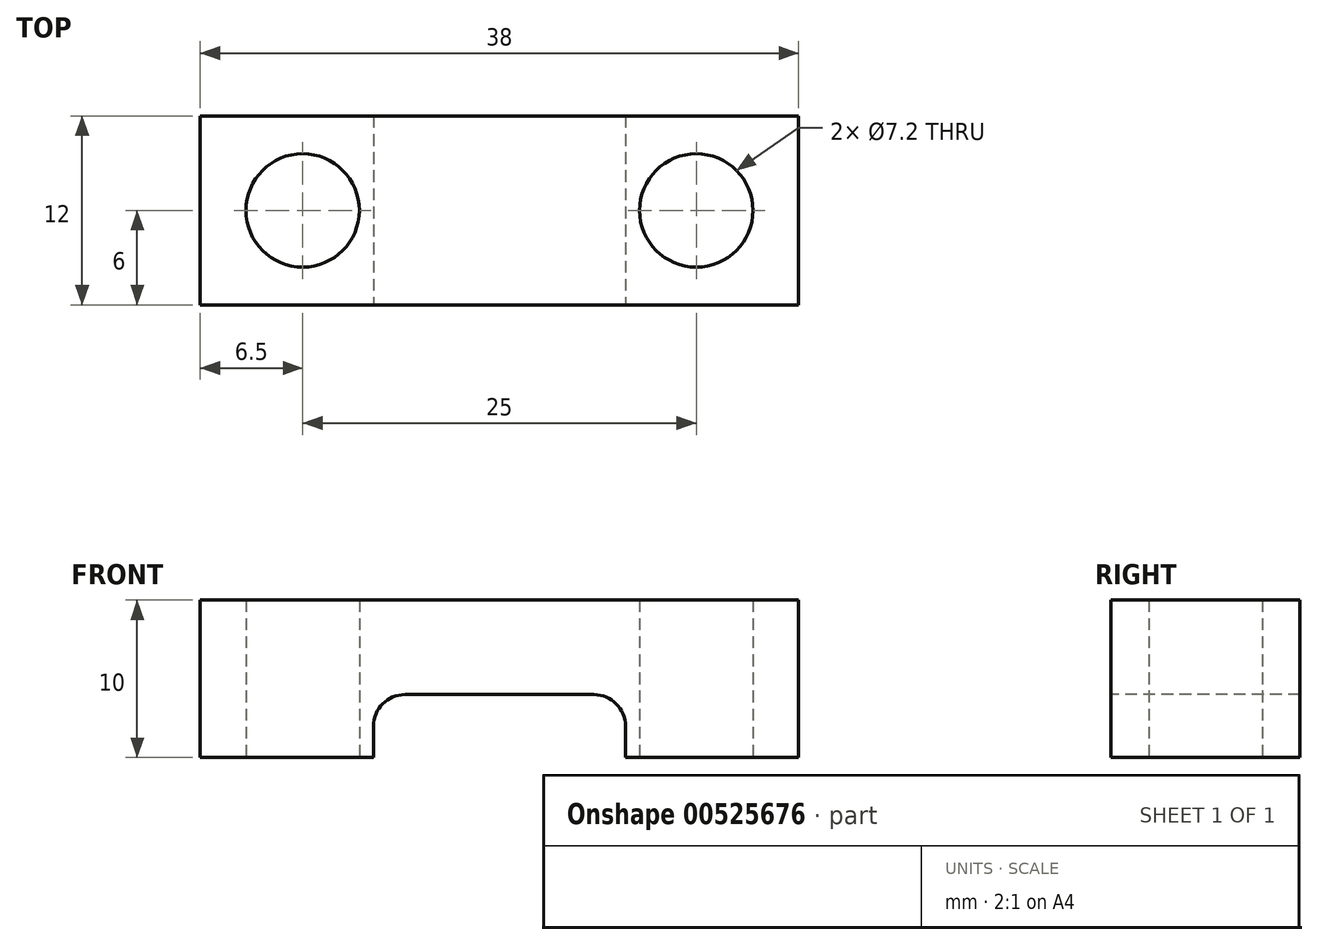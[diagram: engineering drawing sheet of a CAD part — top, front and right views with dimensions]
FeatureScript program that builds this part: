
annotation { "Feature Type Name" : "Feature", "Feature Type Description" : "" }
export const myFeature = defineFeature(function(context is Context, id is Id, definition is map)
    precondition{}
    {
        {
            var Q0;
            Q0=qCreatedBy(makeId("Top.planeOp"),FACE);
            var sketch = newSketch(context, id + "F0", { "sketchPlane" : qUnion([Q0])});
            skLineSegment(sketch, "E0.bottom", {"start": v(-19, 6) * mm, "end": v(19, 6) * mm});
            skLineSegment(sketch, "E0.top", {"start": v(-19, -6) * mm, "end": v(19, -6) * mm});
            skLineSegment(sketch, "E0.left", {"start": v(-19, 6) * mm, "end": v(-19, -6) * mm});
            skLineSegment(sketch, "E0.right", {"start": v(19, 6) * mm, "end": v(19, -6) * mm});
            skCircle(sketch, "E1", {"center": v(-12.5, 0) * mm, "radius": 3.6 * mm});
            skCircle(sketch, "E2", {"center": v(12.5, 0) * mm, "radius": 3.6 * mm});
            skSolve(sketch);
        }
        {
            var Q0;
            Q0=qSketchRegion(id+"F0",true);
            extrude(context, id + "F1", {"entities" : qUnion([Q0]), "depth" : 10 * mm});
        }
        {
            var Q0;
            Q0=makeQuery(id+"F1.opExtrude","SWEPT_FACE",FACE,{"disambiguationData":[OSD([sQuery(id+"F0.wireOp",EDGE,"E0.top")])]});
            var sketch = newSketch(context, id + "F2", { "sketchPlane" : qUnion([Q0])});
            skLineSegment(sketch, "E3.bottom", {"start": v(-8, 0) * mm, "end": v(8, 0) * mm});
            skLineSegment(sketch, "E3.top", {"start": v(-8, 4) * mm, "end": v(8, 4) * mm});
            skLineSegment(sketch, "E3.left", {"start": v(-8, 0) * mm, "end": v(-8, 4) * mm});
            skLineSegment(sketch, "E3.right", {"start": v(8, 0) * mm, "end": v(8, 4) * mm});
            skLineSegment(sketch, "E4", {"start": v(0, 10) * mm, "end": v(0, 0) * mm, "construction": true});
            skSolve(sketch);
        }
        {
            var Q0;
            Q0=qSketchRegion(id+"F2",true);
            extrude(context, id + "F3", {"entities" : qUnion([Q0]), "operationType" : NewBodyOperationType.REMOVE, "endBound" : BoundingType.THROUGH_ALL, "oppositeDirection" : true, "depth" : 25 * mm});
        }
        {
            var Q0;
            Q0=makeQuery(id+"F3.boolean.opBoolean","COPY",EDGE,{"derivedFrom":makeQuery(id+"F3.opExtrude","SWEPT_EDGE",EDGE,{"disambiguationData":[OSD([sQuery(id+"F2.wireOp",EDGE,"E3.top"),sQuery(id+"F2.wireOp",EDGE,"E3.left")])]})});
            var Q1;
            Q1=makeQuery(id+"F3.boolean.opBoolean","COPY",EDGE,{"derivedFrom":makeQuery(id+"F3.opExtrude","SWEPT_EDGE",EDGE,{"disambiguationData":[OSD([sQuery(id+"F2.wireOp",EDGE,"E3.top"),sQuery(id+"F2.wireOp",EDGE,"E3.right")])]})});
            fillet(context, id + "F4", {"entities" : qUnion([Q0, Q1]), "radius" : 2 * mm, "tangentPropagation" : true, "allowEdgeOverflow" : false});
        }
    });
